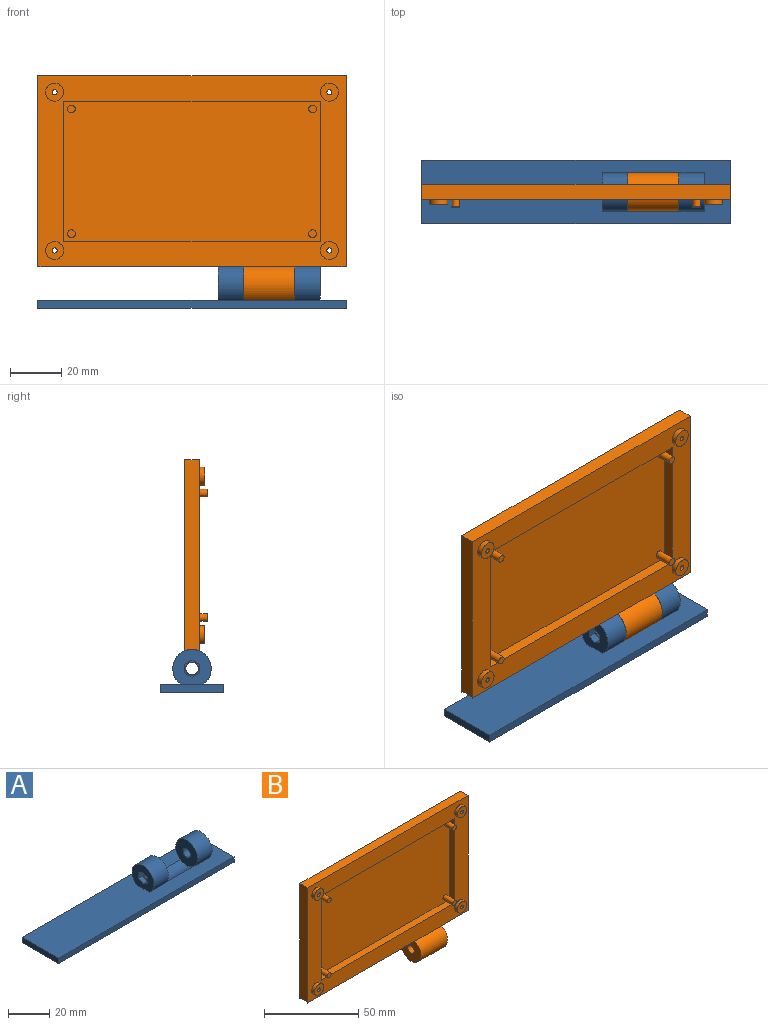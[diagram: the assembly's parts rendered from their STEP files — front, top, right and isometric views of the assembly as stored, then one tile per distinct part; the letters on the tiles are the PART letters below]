
ASSEMBLY  parts=2 mates=1
PART A: 23 faces, bbox 120.5x25x16.8 mm
  f0: plane 15x13.64mm, normal (-1,0,0), area 139.8mm2, adj f4,f5,f16,f17,f18,f19,f20,f21
  f1: cylinder r=2.5mm len=7mm, axis (-1,0,0), area 110mm2, adj f12,f15
  f2: plane 25x3.18mm, normal (1,0,0), area 79.4mm2, adj f5,f7,f8,f9
  f3: cylinder r=7.5mm len=15mm, axis (1,0,0), area 379.6mm2, adj f5,f10,f13
  f4: cylinder r=7.5mm len=15mm, axis (-1,0,0), area 379.6mm2, adj f0,f5,f12
  f5: plane 120.5x25mm, normal (0,0,1), area 2668.3mm2, adj f0,f2,f3,f4,f6,f8,f9,f11
  f6: plane 25x3.18mm, normal (-1,0,0), area 79.4mm2, adj f5,f7,f8,f9
  f7: plane 120.5x25mm, normal (0,0,-1), area 3012.5mm2, adj f2,f6,f8,f9
  f8: plane 120.5x3.18mm, normal (0,-1,0), area 382.6mm2, adj f2,f5,f6,f7
  f9: plane 120.5x3.18mm, normal (0,1,0), area 382.6mm2, adj f2,f5,f6,f7
  f10: plane 15x15mm, normal (-1,0,0), area 157.1mm2, adj f3,f11,f14
  f11: cylinder r=7.5mm len=20mm, axis (1,0,0), area 183.3mm2, adj f5,f10,f12
  f12: plane 15x15mm, normal (1,0,0), area 157.1mm2, adj f1,f4,f5,f11
  f13: plane 15x13.64mm, normal (1,0,0), area 130.3mm2, adj f3,f5,f22
  f14: cylinder r=2.5mm len=9mm, axis (-1,0,0), area 141.4mm2, adj f10,f22
  f15: plane 6.68x5.8mm, normal (-1,0,0), area 9.3mm2, adj f1,f16,f17,f18,f19,f20,f21
  f16: plane 3.34x3mm, normal (0,1,0), area 10mm2, adj f0,f15,f17,f21
  f17: plane 3x2.9mm, normal (0,0.5,-0.87), area 10mm2, adj f0,f15,f16,f18
  f18: plane 3x2.89mm, normal (0,-0.5,-0.86), area 10mm2, adj f0,f15,f17,f19
  f19: plane 3.34x3mm, normal (0,-1,0), area 10mm2, adj f0,f15,f18,f20
  f20: plane 3x2.9mm, normal (0,-0.5,0.87), area 10mm2, adj f0,f15,f19,f21
  f21: plane 3x2.89mm, normal (0,0.5,0.86), area 10mm2, adj f0,f15,f16,f20
  f22: cone r=2.5mm half-angle=45deg, axis (1,0,0), area 26.7mm2, adj f13,f14
PART B: 44 faces, bbox 120.5x15x89.3 mm
  f0: cylinder r=7.5mm len=20mm, axis (-1,0,0), area 822.3mm2, adj f1,f13,f40,f42
  f1: plane 120.5x74.89mm, normal (0,1,0), area 8945.1mm2, adj f0,f6,f7,f8,f31,f33,f35,f37
  f2: cylinder r=1mm len=5.85mm, axis (0,-1,0), area 36.8mm2, adj f30,f38
  f3: cylinder r=1mm len=5.85mm, axis (0,-1,0), area 36.8mm2, adj f28,f36
  f4: cylinder r=1mm len=5.85mm, axis (0,-1,0), area 36.8mm2, adj f26,f34
  f5: cylinder r=1mm len=5.85mm, axis (0,-1,0), area 36.8mm2, adj f24,f32
  f6: plane 74.89x5.85mm, normal (1,0,0), area 435.7mm2, adj f1,f7,f13,f41
  f7: plane 120.5x5.85mm, normal (0,0,1), area 704.9mm2, adj f1,f6,f8,f13
  f8: plane 74.89x5.85mm, normal (-1,0,0), area 435.7mm2, adj f1,f7,f13,f39
  f9: plane 100.5x4.25mm, normal (0,0,-1), area 427.1mm2, adj f10,f12,f13,f14
  f10: plane 54.94x4.25mm, normal (-1,0,0), area 233.5mm2, adj f9,f11,f13,f14
  f11: plane 100.5x4.25mm, normal (0,0,1), area 427.1mm2, adj f10,f12,f13,f14
  f12: plane 54.94x4.25mm, normal (1,0,0), area 233.5mm2, adj f9,f11,f13,f14
  f13: plane 120.5x74.89mm, normal (0,-1,0), area 3348.3mm2, adj f0,f6,f7,f8,f9,f10,f11,f12
  f14: plane 100.5x54.94mm, normal (0,-1,0), area 5493.2mm2, adj f9,f10,f11,f12,f15,f17,f19,f21
  f15: cylinder r=1.5mm len=7.25mm, axis (0,1,0), area 68.3mm2, adj f14,f16
  f16: plane 3x3mm, normal (0,-1,0), area 7.1mm2, adj f15
  f17: cylinder r=1.5mm len=7.25mm, axis (0,1,0), area 68.3mm2, adj f14,f18
  f18: plane 3x3mm, normal (0,-1,0), area 7.1mm2, adj f17
  f19: cylinder r=1.5mm len=7.25mm, axis (0,1,0), area 68.3mm2, adj f14,f20
  f20: plane 3x3mm, normal (0,-1,0), area 7.1mm2, adj f19
  f21: cylinder r=1.5mm len=7.25mm, axis (0,1,0), area 68.3mm2, adj f14,f22
  f22: plane 3x3mm, normal (0,-1,0), area 7.1mm2, adj f21
  f23: cylinder r=3.5mm len=7mm, axis (0,1,0), area 44mm2, adj f13,f24
  f24: plane 7x7mm, normal (0,-1,0), area 35.3mm2, adj f5,f23
  f25: cylinder r=3.5mm len=7mm, axis (0,1,0), area 44mm2, adj f13,f26
  f26: plane 7x7mm, normal (0,-1,0), area 35.3mm2, adj f4,f25
  f27: cylinder r=3.5mm len=7mm, axis (0,1,0), area 44mm2, adj f13,f28
  f28: plane 7x7mm, normal (0,-1,0), area 35.3mm2, adj f3,f27
  f29: cylinder r=3.5mm len=7mm, axis (0,1,0), area 44mm2, adj f13,f30
  f30: plane 7x7mm, normal (0,-1,0), area 35.3mm2, adj f2,f29
  f31: cylinder r=2.5mm len=5mm, axis (0,1,0), area 31.4mm2, adj f1,f32
  f32: plane 5x5mm, normal (0,1,0), area 16.5mm2, adj f5,f31
  f33: cylinder r=2.5mm len=5mm, axis (0,1,0), area 31.4mm2, adj f1,f34
  f34: plane 5x5mm, normal (0,1,0), area 16.5mm2, adj f4,f33
  f35: cylinder r=2.5mm len=5mm, axis (0,1,0), area 31.4mm2, adj f1,f36
  f36: plane 5x5mm, normal (0,1,0), area 16.5mm2, adj f3,f35
  f37: cylinder r=2.5mm len=5mm, axis (0,1,0), area 31.4mm2, adj f1,f38
  f38: plane 5x5mm, normal (0,1,0), area 16.5mm2, adj f2,f37
  f39: cylinder r=7.5mm len=80.5mm, axis (-1,0,0), area 483.8mm2, adj f1,f8,f13,f40
  f40: plane 15x15mm, normal (-1,0,0), area 157.1mm2, adj f0,f39,f43
  f41: cylinder r=7.5mm len=20mm, axis (1,0,0), area 120.2mm2, adj f1,f6,f13,f42
  f42: plane 15x15mm, normal (1,0,0), area 157.1mm2, adj f0,f41,f43
  f43: cylinder r=2.5mm len=20mm, axis (1,0,0), area 314.2mm2, adj f40,f42
PLACE A t=(-24.24,21.16,-39.26)mm
PLACE B t=(-24.24,11.58,12.79)mm
MATE planar A.f3 <-> B.f39  axis (1,0,0) through (-3.99,8.66,-31.53)mm
